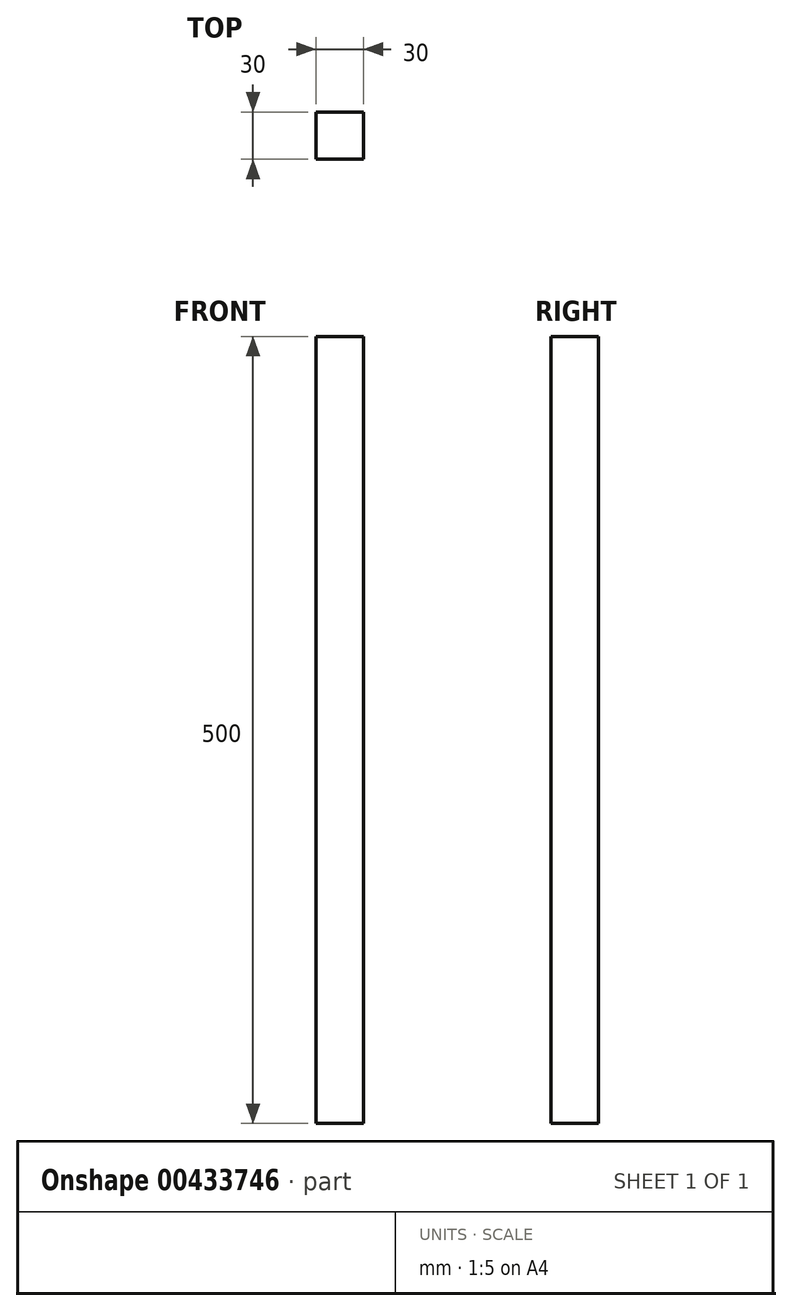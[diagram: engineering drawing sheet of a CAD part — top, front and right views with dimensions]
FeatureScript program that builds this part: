
annotation { "Feature Type Name" : "Feature", "Feature Type Description" : "" }
export const myFeature = defineFeature(function(context is Context, id is Id, definition is map)
    precondition{}
    {
        {
            var Q0;
            Q0=qCreatedBy(makeId("Front.planeOp"),FACE);
            var sketch = newSketch(context, id + "F0", { "sketchPlane" : qUnion([Q0])});
            skLineSegment(sketch, "E0.bottom", {"start": v(-19.67, 425.52) * mm, "end": v(10.33, 425.52) * mm});
            skLineSegment(sketch, "E0.top", {"start": v(-19.67, -74.48) * mm, "end": v(10.33, -74.48) * mm});
            skLineSegment(sketch, "E0.left", {"start": v(-19.67, 425.52) * mm, "end": v(-19.67, -74.48) * mm});
            skLineSegment(sketch, "E0.right", {"start": v(10.33, 425.52) * mm, "end": v(10.33, -74.48) * mm});
            skSolve(sketch);
        }
        {
            var Q0;
            Q0 = qSketchRegion(id + "F0", true);
            extrude(context, id + "F1", {"entities" : qUnion([Q0]), "depth" : 30 * mm, "offsetDistance" : 25 * mm});
        }
    });
